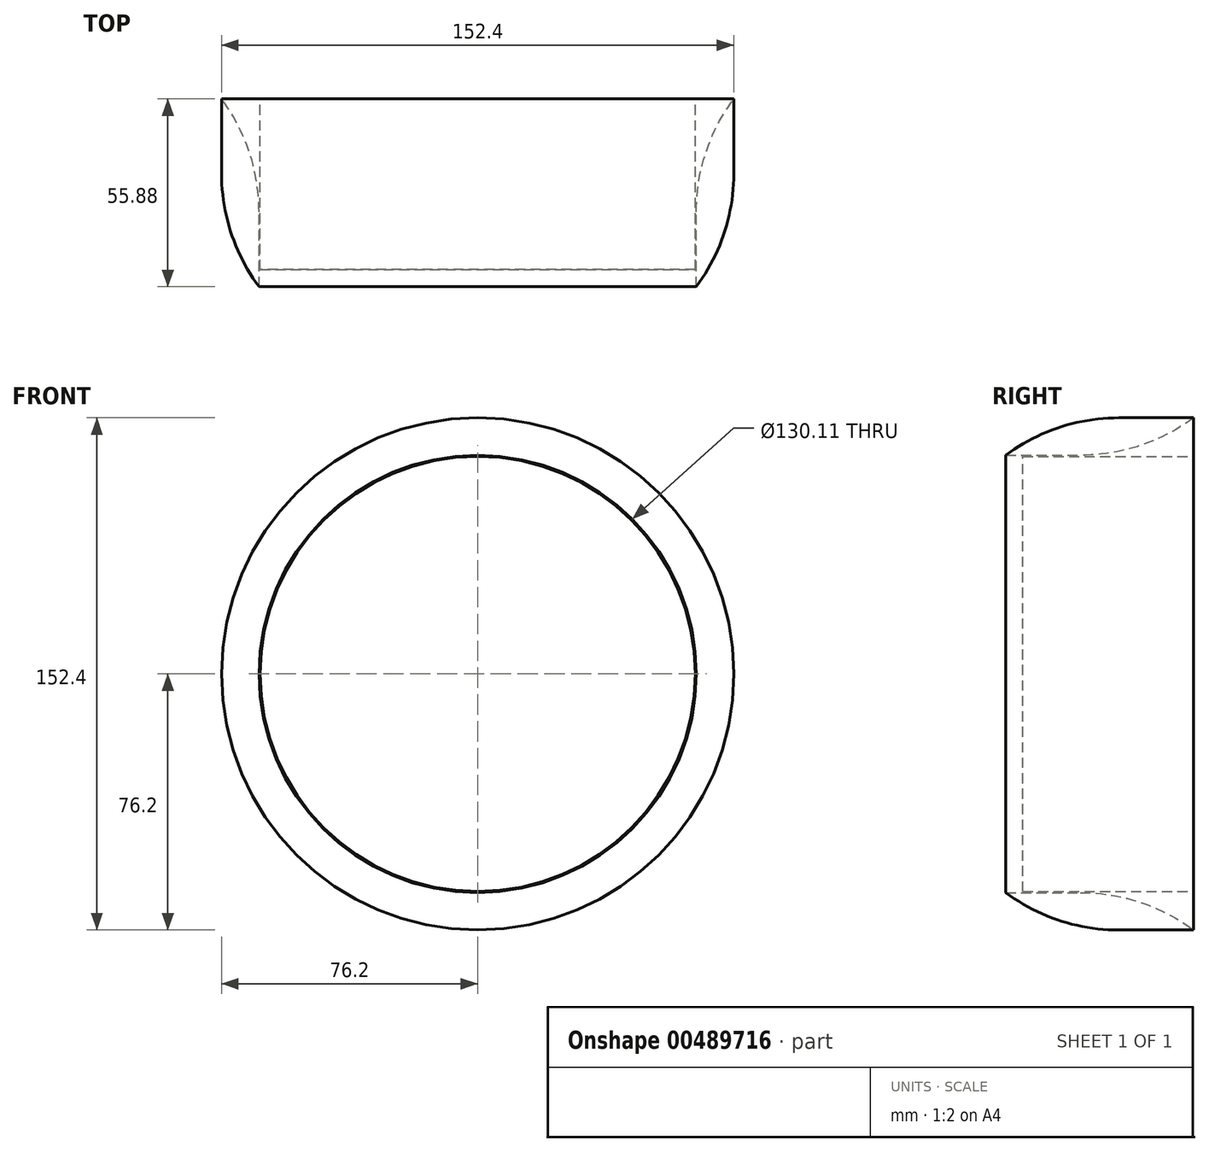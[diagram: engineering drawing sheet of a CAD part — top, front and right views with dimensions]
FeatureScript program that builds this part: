
annotation { "Feature Type Name" : "Feature", "Feature Type Description" : "" }
export const myFeature = defineFeature(function(context is Context, id is Id, definition is map)
    precondition{}
    {
        {
            var Q0;
            Q0=qCreatedBy(makeId("Front.planeOp"),FACE);
            var sketch = newSketch(context, id + "F0", { "sketchPlane" : qUnion([Q0])});
            skLineSegment(sketch, "E0.bottom", {"start": v(-76.2, 76.2) * mm, "end": v(76.2, 76.2) * mm});
            skLineSegment(sketch, "E0.top", {"start": v(-76.2, -76.2) * mm, "end": v(76.2, -76.2) * mm});
            skLineSegment(sketch, "E0.left", {"start": v(-76.2, 76.2) * mm, "end": v(-76.2, -76.2) * mm});
            skLineSegment(sketch, "E0.right", {"start": v(76.2, 76.2) * mm, "end": v(76.2, -76.2) * mm});
            skPoint(sketch, "E0.middle", {"position": v(0, 0) * mm});
            skCircle(sketch, "E1", {"center": v(0, 0) * mm, "radius": 76.2 * mm});
            skCircle(sketch, "E2", {"center": v(0, 0) * mm, "radius": 65.06 * mm});
            skSolve(sketch);
        }
        {
            var Q0;
            {var subQ0=sQuery(id+"F0.wireOp",EDGE,"E1");var subQ1=makeQuery(id+"F0.imprint","INTERSECT",VERTEX,{"derivedFrom":[sQuery(id+"F0.wireOp",EDGE,"E0.bottom"),subQ0]});Q0=makeQuery(id+"F0.imprint","IMPRINT",FACE,{"disambiguationData":[TD([[makeQuery(id+"F0.imprint","IMPRINT",EDGE,{"disambiguationData":[TD([[subQ1,1.0]])],"derivedFrom":subQ0}),1.0]])]});}
            extrude(context, id + "F1", {"entities" : qUnion([Q0]), "depth" : 55.88 * mm});
        }
        {
            var Q0;
            Q0=makeQuery(id+"F1.opExtrude","CAP_EDGE",EDGE,{"disambiguationData":[OSD([sQuery(id+"F0.wireOp",EDGE,"E1")])],"isStart":false});
            var Q1;
            Q1=makeQuery(id+"F1.opExtrude","CAP_EDGE",EDGE,{"disambiguationData":[OSD([sQuery(id+"F0.wireOp",EDGE,"E2")])],"isStart":true});
            fillet(context, id + "F2", {"entities" : qUnion([Q0, Q1]), "radius" : 56.42 * mm, "tangentPropagation" : true, "allowEdgeOverflow" : false});
        }
        {
            var Q0;
            Q0=makeQuery(id+"F0.imprint","IMPRINT",FACE,{"disambiguationData":[TD([[makeQuery(id+"F0.imprint","IMPRINT",EDGE,{"derivedFrom":sQuery(id+"F0.wireOp",EDGE,"E2")}),1.0]])]});
            var sketch = newSketch(context, id + "F3", { "sketchPlane" : qUnion([Q0])});
            skCircle(sketch, "E3", {"center": v(0, 0) * mm, "radius": 64.74 * mm});
            skSolve(sketch);
        }
        {
            var Q0;
            Q0=makeQuery(id+"F3.imprint","IMPRINT",FACE,{"disambiguationData":[TD([[makeQuery(id+"F3.imprint","IMPRINT",EDGE,{"derivedFrom":sQuery(id+"F3.wireOp",EDGE,"E3")}),1.0]])]});
            extrude(context, id + "F4", {"entities" : qUnion([Q0]), "depth" : 50.8 * mm});
        }
    });
